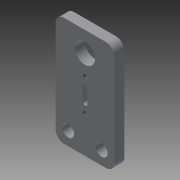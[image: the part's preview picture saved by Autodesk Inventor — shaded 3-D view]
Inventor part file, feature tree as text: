
AUTODESK INVENTOR PART (.ipt)
format: ipt  version: 2015 SP1 (Build 190203100, 203)  size: 121,856 bytes
history: native  units: in
note: dims shown in document units (in); Inventor stores cm internally (conversion verified against a paired STEP export)
features: sketch x1, extrude x1, hole x1, fillet x1
ambient origin geometry x8: Origin, YZ Plane, XZ Plane, XY Plane, X Axis, Y Axis, Z Axis, Center Point
bodies: Body1 (feature_tree)
feature tree (4):
  sketch  "Sketch1"  dims[d3=1.378in d4=0.2756in d6=0.2756in d12=0.4724in d13=0.4724in d25=0.0968in d26=0.2362in d27=0.119in d28=0.0787in d29=0.5635in d30=0.3465in d31=0.8108in d36=0.0591in d37=0.315in d38=0.748in d39=0.4724in d42=0.5512in d43=0.7874in d44=0.2362in d45=0.0in d46=0.1969in d48=0.315in]
  extrude  "Extrusion4"  Depth=0.1969in
  hole  "Hole1"  [1 undecoded]
  fillet  "Fillet3"  Radius=0.4724in
note: 1 required parameter value undecoded (feature->parameter linkage not recoverable at this tier; creation-order binding heuristic only, values carry confidence <= 0.55)
